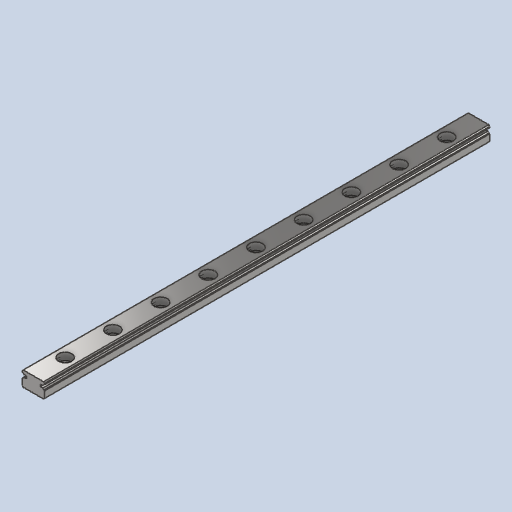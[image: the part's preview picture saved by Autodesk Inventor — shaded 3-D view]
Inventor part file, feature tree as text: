
AUTODESK INVENTOR PART (.ipt)
format: ipt  version: 2023 (Build 270158000, 158)  size: 202,240 bytes
history: native  units: mm
features: other x77, sketch x2, extrude x1, hole x1, pattern_linear x1
ambient origin geometry x8: Origin, YZ Plane, XZ Plane, XY Plane, X Axis, Y Axis, Z Axis, Center Point
bodies: Solid1 (feature_tree)
feature tree (82):
  extrude  "Extrusion1"  Depth=10.0mm TaperAngle=0.0deg
  hole  "Hole1"  [1 undecoded]
  pattern_linear  "Rectangular Pattern1"  [2 undecoded]
  other  "to_block_XY"
  other  "to_block_YZ"
  other  "to_block_ZX"
  other  "to_block_X"
  other  "to_block_Y"
  other  "to_block_Z"
  other  "to_block_Center"
  other  "to_block_2_XY"
  other  "to_block_2_YZ"
  other  "to_block_2_ZX"
  other  "to_block_2_X"
  other  "to_block_2_Y"
  other  "to_block_2_Z"
  other  "to_block_2_Center"
  other  "to_bolt_1_XY"
  other  "to_bolt_1_YZ"
  other  "to_bolt_1_ZX"
  other  "to_bolt_1_X"
  other  "to_bolt_1_Y"
  other  "to_bolt_1_Z"
  other  "to_bolt_1_Center"
  other  "to_bolt_2_XY"
  other  "to_bolt_2_YZ"
  other  "to_bolt_2_ZX"
  other  "to_bolt_2_X"
  other  "to_bolt_2_Y"
  other  "to_bolt_2_Z"
  other  "to_bolt_2_Center"
  other  "to_bolt_3_XY"
  other  "to_bolt_3_YZ"
  other  "to_bolt_3_ZX"
  other  "to_bolt_3_X"
  other  "to_bolt_3_Y"
  other  "to_bolt_3_Z"
  other  "to_bolt_3_Center"
  other  "to_bolt_4_XY"
  other  "to_bolt_4_YZ"
  other  "to_bolt_4_ZX"
  other  "to_bolt_4_X"
  other  "to_bolt_4_Y"
  other  "to_bolt_4_Z"
  other  "to_bolt_4_Center"
  other  "to_bolt_5_XY"
  other  "to_bolt_5_YZ"
  other  "to_bolt_5_ZX"
  other  "to_bolt_5_X"
  other  "to_bolt_5_Y"
  other  "to_bolt_5_Z"
  other  "to_bolt_5_Center"
  other  "to_bolt_6_XY"
  other  "to_bolt_6_YZ"
  other  "to_bolt_6_ZX"
  other  "to_bolt_6_X"
  other  "to_bolt_6_Y"
  other  "to_bolt_6_Z"
  other  "to_bolt_6_Center"
  other  "to_bolt_7_XY"
  other  "to_bolt_7_YZ"
  other  "to_bolt_7_ZX"
  other  "to_bolt_7_X"
  other  "to_bolt_7_Y"
  other  "to_bolt_7_Z"
  other  "to_bolt_7_Center"
  other  "to_bolt_8_XY"
  other  "to_bolt_8_YZ"
  other  "to_bolt_8_ZX"
  other  "to_bolt_8_X"
  other  "to_bolt_8_Y"
  other  "to_bolt_8_Z"
  other  "to_bolt_8_Center"
  other  "to_bolt_9_XY"
  other  "to_bolt_9_YZ"
  other  "to_bolt_9_ZX"
  other  "to_bolt_9_X"
  other  "to_bolt_9_Y"
  other  "to_bolt_9_Z"
  other  "to_bolt_9_Center"
  sketch  "Sketch_12"  dims[d2=2.4mm d3=6.0mm d4=4.2mm d5=2.3mm d6=90.0deg d7=4.7mm d8=0.0mm d9=90.0mm d11=15.0mm d12=10.0mm d14=0.0mm d15=0.0mm d16=0.0mm d17=0.0mm d18=0.0mm d19=0.0mm d20=0.0mm d21=0.0mm d22=0.0mm d23=0.0mm]
  sketch  "Sketch2"  dims[d0=140.0mm d1=0.0mm]
note: 3 required parameter values undecoded (feature->parameter linkage not recoverable at this tier; creation-order binding heuristic only, values carry confidence <= 0.55)
